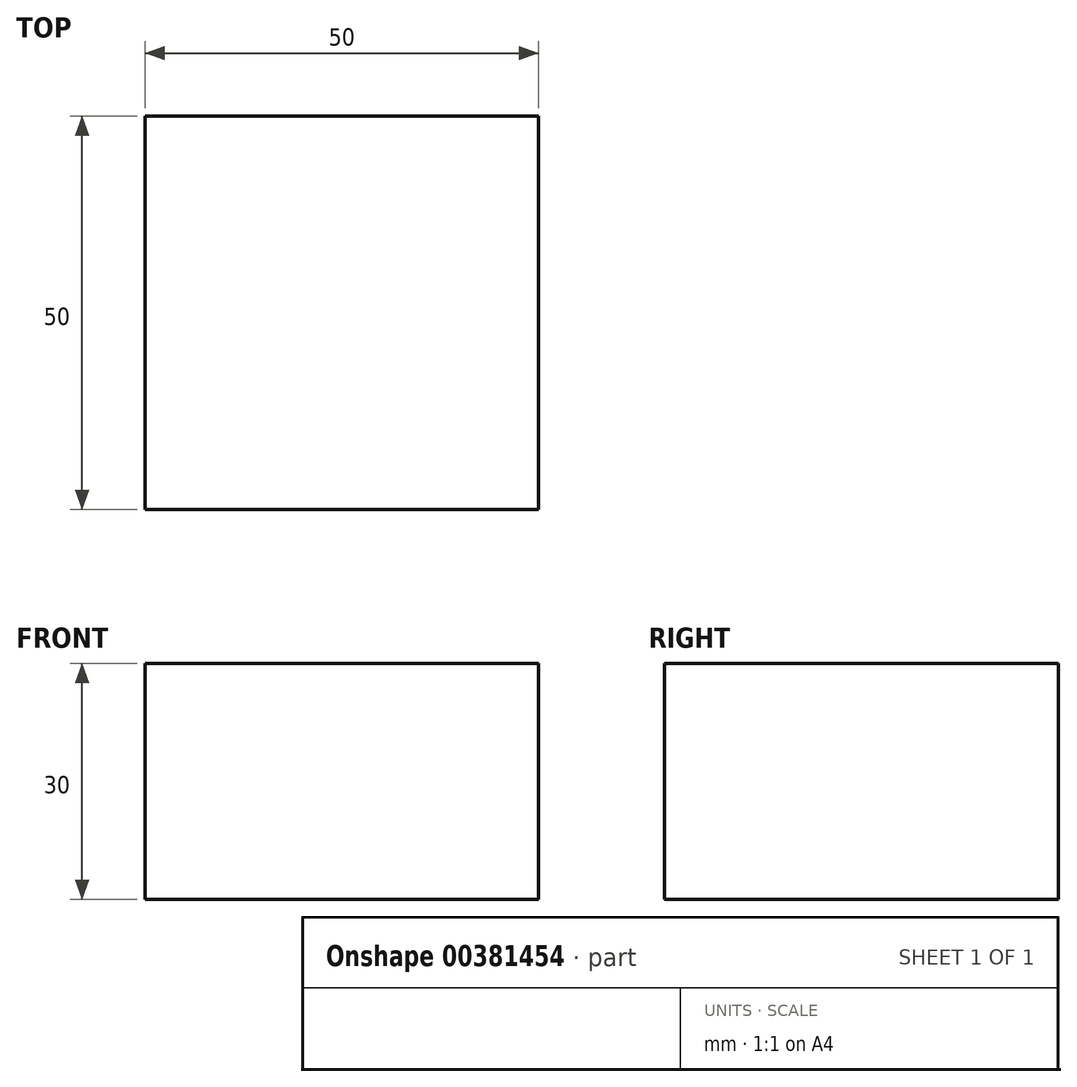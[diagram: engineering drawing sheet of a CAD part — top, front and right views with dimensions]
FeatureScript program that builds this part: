
annotation { "Feature Type Name" : "Feature", "Feature Type Description" : "" }
export const myFeature = defineFeature(function(context is Context, id is Id, definition is map)
    precondition{}
    {
        {
            var Q0;
            Q0=qCreatedBy(makeId("Top.planeOp"),FACE);
            var sketch = newSketch(context, id + "F0", { "sketchPlane" : qUnion([Q0])});
            skLineSegment(sketch, "E0.bottom", {"start": v(0, 0) * mm, "end": v(50, 0) * mm});
            skLineSegment(sketch, "E0.top", {"start": v(0, 50) * mm, "end": v(50, 50) * mm});
            skLineSegment(sketch, "E0.left", {"start": v(0, 0) * mm, "end": v(0, 50) * mm});
            skLineSegment(sketch, "E0.right", {"start": v(50, 0) * mm, "end": v(50, 50) * mm});
            skArc(sketch, "E1", {"start": v(40, 0) * mm, "mid": v(42.93, 7.07) * mm, "end": v(50, 10) * mm});
            skArc(sketch, "E2", {"start": v(10, 0) * mm, "mid": v(21.72, 28.28) * mm, "end": v(50, 40) * mm});
            skSolve(sketch);
        }
        {
            var Q0;
            Q0=qCreatedBy(makeId("Front.planeOp"),FACE);
            var sketch = newSketch(context, id + "F1", { "sketchPlane" : qUnion([Q0])});
            skLineSegment(sketch, "E3.bottom", {"start": v(0, 0) * mm, "end": v(50, 0) * mm});
            skLineSegment(sketch, "E3.top", {"start": v(0, -30) * mm, "end": v(50, -30) * mm});
            skLineSegment(sketch, "E3.left", {"start": v(0, 0) * mm, "end": v(0, -30) * mm});
            skLineSegment(sketch, "E3.right", {"start": v(50, 0) * mm, "end": v(50, -30) * mm});
            skLineSegment(sketch, "E4", {"start": v(10, 0) * mm, "end": v(28.4, -18.4) * mm});
            skLineSegment(sketch, "E5", {"start": v(36.83, -15.84) * mm, "end": v(40, 0) * mm});
            skPoint(sketch, "E6.visualSharp", {"position": v(35, -25) * mm});
            skArc(sketch, "E6.filletArc", {"start": v(28.4, -18.4) * mm, "mid": v(33.38, -19.64) * mm, "end": v(36.83, -15.84) * mm});
            skSolve(sketch);
        }
        {
            var Q0;
            Q0=qCreatedBy(makeId("Right.planeOp"),FACE);
            cPlane(context, id + "F2", {"entities" : qUnion([Q0]), "cplaneType" : CPlaneType.OFFSET, "offset" : 50 * mm, "width" : 150 * mm, "height" : 150 * mm});
        }
        {
            var Q0;
            Q0=qCreatedBy(id+"F2.planeOp",FACE);
            var sketch = newSketch(context, id + "F3", { "sketchPlane" : qUnion([Q0])});
            skLineSegment(sketch, "E7.bottom", {"start": v(0, 0) * mm, "end": v(50, 0) * mm});
            skLineSegment(sketch, "E7.top", {"start": v(0, -30) * mm, "end": v(50, -30) * mm});
            skLineSegment(sketch, "E7.left", {"start": v(0, 0) * mm, "end": v(0, -30) * mm});
            skLineSegment(sketch, "E7.right", {"start": v(50, 0) * mm, "end": v(50, -30) * mm});
            skLineSegment(sketch, "E8", {"start": v(10, 0) * mm, "end": v(24.31, -8.59) * mm});
            skLineSegment(sketch, "E9", {"start": v(38.94, -3.17) * mm, "end": v(40, 0) * mm});
            skPoint(sketch, "E10.visualSharp", {"position": v(35, -15) * mm});
            skArc(sketch, "E10.filletArc", {"start": v(24.31, -8.59) * mm, "mid": v(32.92, -9.4) * mm, "end": v(38.94, -3.17) * mm});
            skSolve(sketch);
        }
        {
            var Q0;
            Q0=qCreatedBy(makeId("Top.planeOp"),FACE);
            var sketch = newSketch(context, id + "F4", { "sketchPlane" : qUnion([Q0])});
            skLineSegment(sketch, "E11.bottom", {"start": v(0, 0) * mm, "end": v(50, 0) * mm});
            skLineSegment(sketch, "E11.top", {"start": v(0, 50) * mm, "end": v(50, 50) * mm});
            skLineSegment(sketch, "E11.left", {"start": v(0, 0) * mm, "end": v(0, 50) * mm});
            skLineSegment(sketch, "E11.right", {"start": v(50, 0) * mm, "end": v(50, 50) * mm});
            skSolve(sketch);
        }
        {
            var Q0;
            Q0 = qSketchRegion(id + "F4", true);
            extrude(context, id + "F5", {"entities" : qUnion([Q0]), "oppositeDirection" : true, "depth" : 30 * mm});
        }
        {
            var Q1;
            {var subQ0=sQuery(id+"F1.wireOp",EDGE,"E4");Q1=makeQuery(id+"F1.imprint","IMPRINT",FACE,{"disambiguationData":[TD([[makeQuery(id+"F1.imprint","IMPRINT",EDGE,{"derivedFrom":subQ0}),1.0]])]});}
            var Q2;
            {var subQ0=sQuery(id+"F3.wireOp",EDGE,"E8");Q2=makeQuery(id+"F3.imprint","IMPRINT",FACE,{"disambiguationData":[TD([[makeQuery(id+"F3.imprint","IMPRINT",EDGE,{"derivedFrom":subQ0}),1.0]])]});}
            var Q3;
            Q3=sQuery(id+"F0.wireOp",EDGE,"E2");
            loft(context, id + "F6", {"operationType" : NewBodyOperationType.ADD, "addGuides" : true, "sheetProfilesArray" : [{ "sheetProfileEntities" : qUnion([Q1]) }, { "sheetProfileEntities" : qUnion([Q2]) }], "guidesArray" : [{ "guideEntities" : qUnion([Q3]), "guideDerivativeType" : LoftGuideDerivativeType.DEFAULT, "guideDerivativeMagnitude" : 1 }]});
        }
    });
